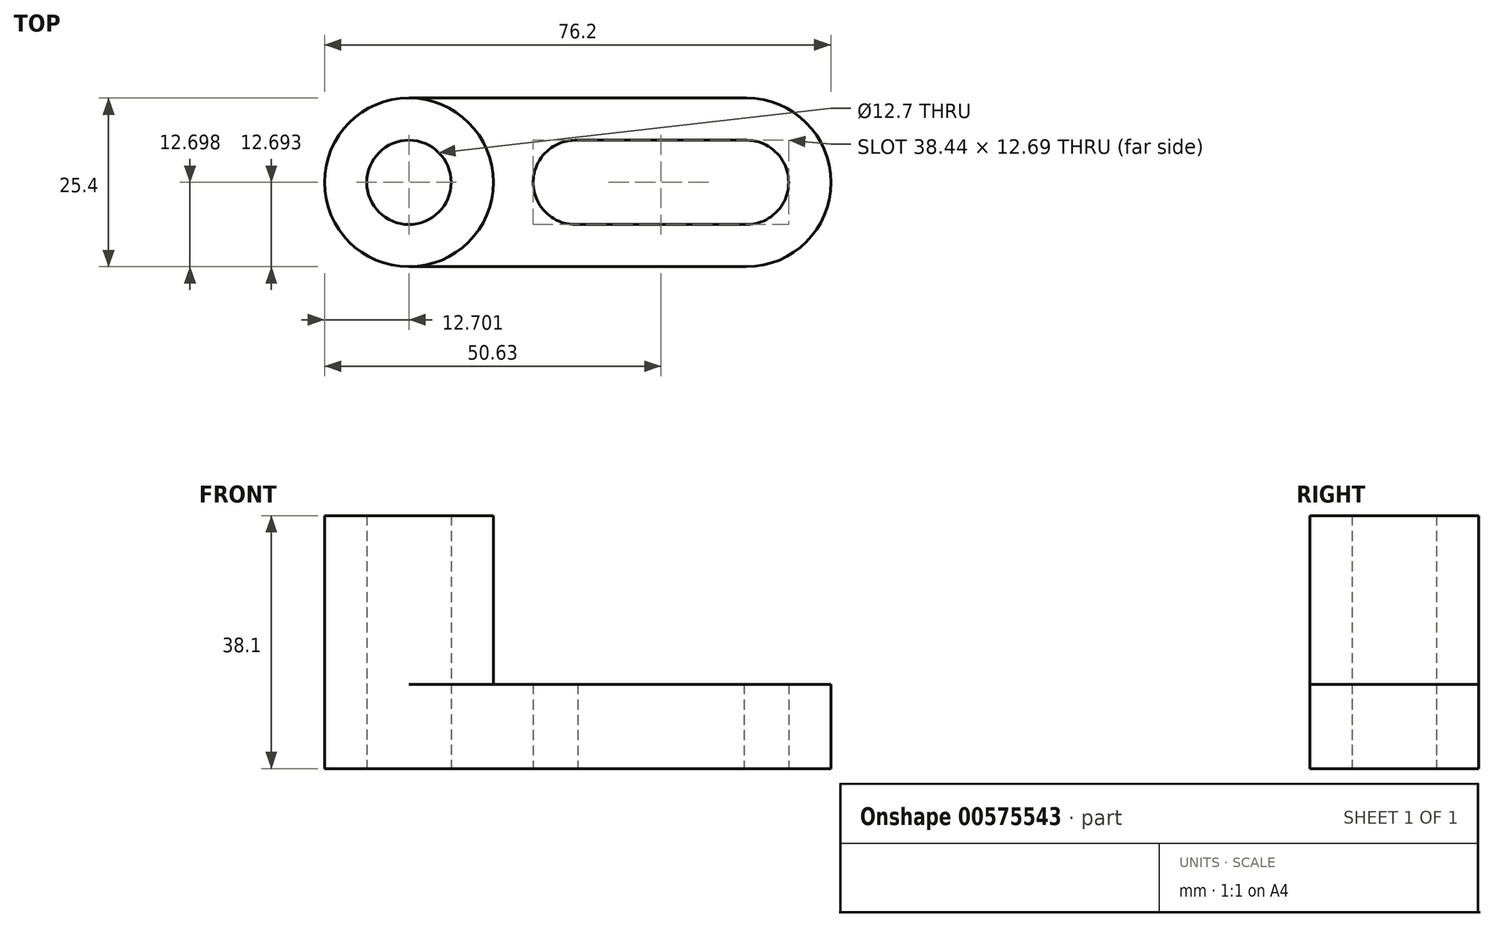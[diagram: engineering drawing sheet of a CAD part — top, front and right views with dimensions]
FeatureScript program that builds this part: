
annotation { "Feature Type Name" : "Feature", "Feature Type Description" : "" }
export const myFeature = defineFeature(function(context is Context, id is Id, definition is map)
    precondition{}
    {
        {
            var Q0;
            Q0=qCreatedBy(makeId("Top.planeOp"),FACE);
            var sketch = newSketch(context, id + "F0", { "sketchPlane" : qUnion([Q0])});
            skLineSegment(sketch, "E0.bottom", {"start": v(-69.49, 47.4) * mm, "end": v(-18.69, 47.4) * mm});
            skLineSegment(sketch, "E0.top", {"start": v(-69.49, 22) * mm, "end": v(-18.69, 22) * mm});
            skLineSegment(sketch, "E0.left", {"start": v(-69.49, 47.4) * mm, "end": v(-69.49, 22) * mm});
            skLineSegment(sketch, "E0.right", {"start": v(-18.69, 47.4) * mm, "end": v(-18.69, 22) * mm});
            skArc(sketch, "E1", {"start": v(-18.69, 47.4) * mm, "mid": v(-5.99, 34.7) * mm, "end": v(-18.69, 22) * mm});
            skArc(sketch, "E2", {"start": v(-69.49, 47.4) * mm, "mid": v(-82.19, 34.7) * mm, "end": v(-69.49, 22) * mm});
            skCircle(sketch, "E3", {"center": v(-69.49, 34.7) * mm, "radius": 12.7 * mm});
            skCircle(sketch, "E4", {"center": v(-18.69, 34.7) * mm, "radius": 6.35 * mm});
            skCircle(sketch, "E5", {"center": v(-44.43, 34.7) * mm, "radius": 6.35 * mm});
            skLineSegment(sketch, "E6", {"start": v(-44.77, 41.04) * mm, "end": v(-19.03, 41.04) * mm});
            skLineSegment(sketch, "E7", {"start": v(-19.03, 41.04) * mm, "end": v(-19.03, 28.36) * mm});
            skLineSegment(sketch, "E8", {"start": v(-19.03, 28.36) * mm, "end": v(-44.43, 28.35) * mm});
            skLineSegment(sketch, "E9", {"start": v(-44.43, 28.35) * mm, "end": v(-44.77, 41.04) * mm});
            skCircle(sketch, "E10", {"center": v(-69.49, 34.7) * mm, "radius": 6.35 * mm});
            skSolve(sketch);
        }
        {
            var Q0;
            {var subQ1=sQuery(id+"F0.wireOp",EDGE,"E0.left");var subQ3=sQuery(id+"F0.wireOp",EDGE,"E10");var subQ4=makeQuery(id+"F0.imprint","INTERSECT",VERTEX,{"disambiguationData":[OD(0.0)],"derivedFrom":[subQ1,subQ3]});Q0=makeQuery(id+"F0.imprint","IMPRINT",FACE,{"disambiguationData":[TD([[makeQuery(id+"F0.imprint","IMPRINT",EDGE,{"disambiguationData":[TD([[subQ4,1.0]])],"derivedFrom":subQ3}),-1.0]])]});}
            var Q1;
            {var subQ1=sQuery(id+"F0.wireOp",EDGE,"E0.left");var subQ3=sQuery(id+"F0.wireOp",EDGE,"E10");var subQ4=makeQuery(id+"F0.imprint","INTERSECT",VERTEX,{"disambiguationData":[OD(0.0)],"derivedFrom":[subQ1,subQ3]});Q1=makeQuery(id+"F0.imprint","IMPRINT",FACE,{"disambiguationData":[TD([[makeQuery(id+"F0.imprint","IMPRINT",EDGE,{"disambiguationData":[TD([[subQ4,-1.0]])],"derivedFrom":subQ3}),-1.0]])]});}
            extrude(context, id + "F1", {"entities" : qUnion([Q0, Q1]), "depth" : 38.1 * mm, "offsetDistance" : 25.4 * mm});
        }
        {
            var Q0;
            Q0 = qSketchRegion(id + "F0", true);
            extrude(context, id + "F2", {"entities" : qUnion([Q0]), "operationType" : NewBodyOperationType.ADD, "depth" : 12.7 * mm, "offsetDistance" : 25.4 * mm});
        }
    });
